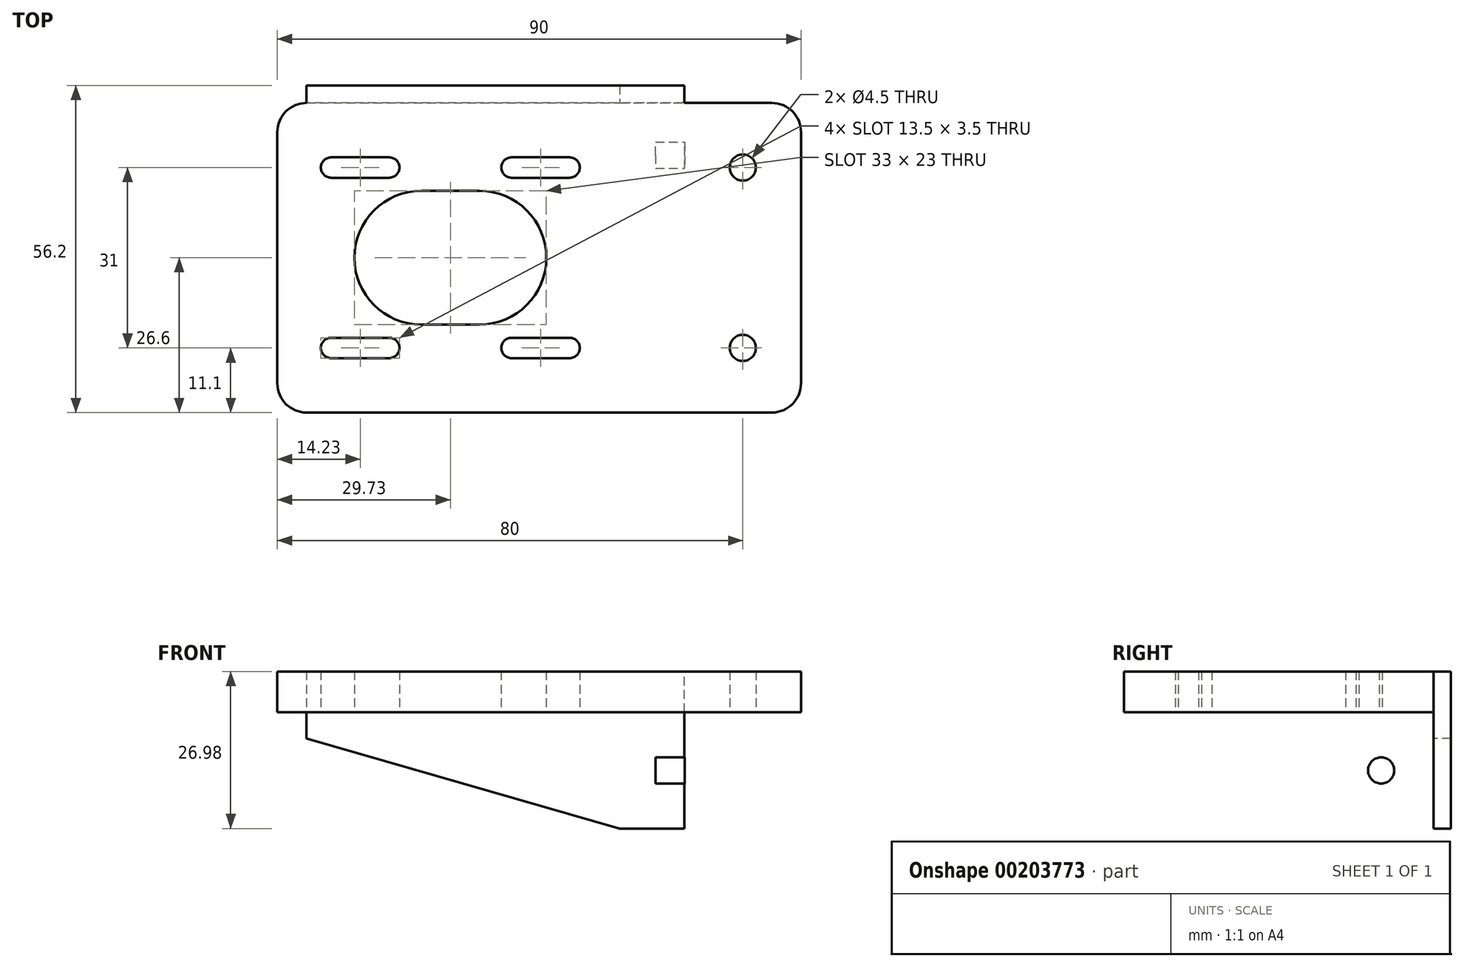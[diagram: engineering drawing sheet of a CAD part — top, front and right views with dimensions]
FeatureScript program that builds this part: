
annotation { "Feature Type Name" : "Feature", "Feature Type Description" : "" }
export const myFeature = defineFeature(function(context is Context, id is Id, definition is map)
    precondition{}
    {
        {
            var Q0;
            Q0=qCreatedBy(makeId("Top.planeOp"),FACE);
            var sketch = newSketch(context, id + "F0", { "sketchPlane" : qUnion([Q0])});
            skLineSegment(sketch, "E0.bottom", {"start": v(45, 26.6) * mm, "end": v(-45, 26.6) * mm});
            skLineSegment(sketch, "E0.top", {"start": v(45, -26.6) * mm, "end": v(-45, -26.6) * mm});
            skLineSegment(sketch, "E0.left", {"start": v(45, 26.6) * mm, "end": v(45, -26.6) * mm});
            skLineSegment(sketch, "E0.right", {"start": v(-45, 26.6) * mm, "end": v(-45, -26.6) * mm});
            skPoint(sketch, "E0.middle", {"position": v(0, 0) * mm});
            skLineSegment(sketch, "E1", {"start": v(-45, 0) * mm, "end": v(-10.27, 0) * mm, "construction": true});
            skLineSegment(sketch, "E2", {"start": v(-10.27, 0) * mm, "end": v(-10.27, 15.5) * mm, "construction": true});
            skLineSegment(sketch, "E3", {"start": v(-10.27, 15.5) * mm, "end": v(5.23, 15.5) * mm, "construction": true});
            skLineSegment(sketch, "E4", {"start": v(5.23, 15.5) * mm, "end": v(35, 15.5) * mm, "construction": true});
            skArc(sketch, "E5", {"start": v(-10.27, -11.5) * mm, "mid": v(1.23, 0) * mm, "end": v(-10.27, 11.5) * mm});
            skArc(sketch, "E6", {"start": v(5.23, 13.75) * mm, "mid": v(6.98, 15.5) * mm, "end": v(5.23, 17.25) * mm});
            skCircle(sketch, "E7", {"center": v(35, 15.5) * mm, "radius": 2.25 * mm});
            skCircle(sketch, "E8.MirrorC", {"center": v(35, -15.5) * mm, "radius": 2.25 * mm});
            skLineSegment(sketch, "E9", {"start": v(-10.27, 11.5) * mm, "end": v(-20.27, 11.5) * mm});
            skLineSegment(sketch, "E10.MirrorCS", {"start": v(-10.27, -11.5) * mm, "end": v(-20.27, -11.5) * mm});
            skArc(sketch, "E11", {"start": v(-20.27, 11.5) * mm, "mid": v(-31.77, 0) * mm, "end": v(-20.27, -11.5) * mm});
            skLineSegment(sketch, "E12", {"start": v(5.23, 15.5) * mm, "end": v(5.23, 10.19) * mm, "construction": true});
            skLineSegment(sketch, "E13", {"start": v(5.23, 13.75) * mm, "end": v(-4.77, 13.75) * mm});
            skLineSegment(sketch, "E14.MirrorCS", {"start": v(5.23, 17.25) * mm, "end": v(-4.77, 17.25) * mm});
            skLineSegment(sketch, "E15", {"start": v(-4.77, 13.75) * mm, "end": v(-4.77, 20.1) * mm, "construction": true});
            skArc(sketch, "E16", {"start": v(-4.77, 17.25) * mm, "mid": v(-6.52, 15.5) * mm, "end": v(-4.77, 13.75) * mm});
            skLineSegment(sketch, "E17", {"start": v(-15.27, 11.5) * mm, "end": v(-15.27, 24.74) * mm, "construction": true});
            skLineSegment(sketch, "E18.MirrorCS", {"start": v(-35.77, 13.75) * mm, "end": v(-25.77, 13.75) * mm});
            skArc(sketch, "E19.MirrorCS", {"start": v(-35.77, 13.75) * mm, "mid": v(-37.52, 15.5) * mm, "end": v(-35.77, 17.25) * mm});
            skLineSegment(sketch, "E20.MirrorCS", {"start": v(-35.77, 17.25) * mm, "end": v(-25.77, 17.25) * mm});
            skArc(sketch, "E21.MirrorCS", {"start": v(-25.77, 17.25) * mm, "mid": v(-24.02, 15.5) * mm, "end": v(-25.77, 13.75) * mm});
            skArc(sketch, "E22.MirrorCS", {"start": v(5.23, -13.75) * mm, "mid": v(6.98, -15.5) * mm, "end": v(5.23, -17.25) * mm});
            skLineSegment(sketch, "E23.MirrorCS", {"start": v(5.23, -17.25) * mm, "end": v(-4.77, -17.25) * mm});
            skArc(sketch, "E24.MirrorCS", {"start": v(-4.77, -17.25) * mm, "mid": v(-6.52, -15.5) * mm, "end": v(-4.77, -13.75) * mm});
            skLineSegment(sketch, "E25.MirrorCS", {"start": v(5.23, -13.75) * mm, "end": v(-4.77, -13.75) * mm});
            skArc(sketch, "E26.MirrorCS", {"start": v(-35.77, -13.75) * mm, "mid": v(-37.52, -15.5) * mm, "end": v(-35.77, -17.25) * mm});
            skLineSegment(sketch, "E27.MirrorCS", {"start": v(-35.77, -13.75) * mm, "end": v(-25.77, -13.75) * mm});
            skArc(sketch, "E28.MirrorCS", {"start": v(-25.77, -17.25) * mm, "mid": v(-24.02, -15.5) * mm, "end": v(-25.77, -13.75) * mm});
            skLineSegment(sketch, "E29.MirrorCS", {"start": v(-35.77, -17.25) * mm, "end": v(-25.77, -17.25) * mm});
            skSolve(sketch);
        }
        {
            var Q0;
            Q0=makeQuery(id+"F0.imprint","IMPRINT",FACE,{"disambiguationData":[TD([[makeQuery(id+"F0.imprint","IMPRINT",EDGE,{"derivedFrom":sQuery(id+"F0.wireOp",EDGE,"E0.bottom")}),1.0]])]});
            extrude(context, id + "F1", {"entities" : qUnion([Q0]), "depth" : 7 * mm, "symmetric" : true});
        }
        {
            var Q0;
            Q0=makeQuery(id+"F1.opExtrude","SWEPT_EDGE",EDGE,{"disambiguationData":[OSD([sQuery(id+"F0.wireOp",EDGE,"E0.bottom"),sQuery(id+"F0.wireOp",EDGE,"E0.right")])]});
            var Q1;
            Q1=makeQuery(id+"F1.opExtrude","SWEPT_EDGE",EDGE,{"disambiguationData":[OSD([sQuery(id+"F0.wireOp",EDGE,"E0.top"),sQuery(id+"F0.wireOp",EDGE,"E0.right")])]});
            var Q2;
            Q2=makeQuery(id+"F1.opExtrude","SWEPT_EDGE",EDGE,{"disambiguationData":[OSD([sQuery(id+"F0.wireOp",EDGE,"E0.top"),sQuery(id+"F0.wireOp",EDGE,"E0.left")])]});
            var Q3;
            Q3=makeQuery(id+"F1.opExtrude","SWEPT_EDGE",EDGE,{"disambiguationData":[OSD([sQuery(id+"F0.wireOp",EDGE,"E0.bottom"),sQuery(id+"F0.wireOp",EDGE,"E0.left")])]});
            fillet(context, id + "F2", {"entities" : qUnion([Q0, Q1, Q2, Q3]), "radius" : 5 * mm, "tangentPropagation" : true, "allowEdgeOverflow" : false});
        }
        {
            var Q0;
            Q0=qCreatedBy(makeId("Front.planeOp"),FACE);
            var sketch = newSketch(context, id + "F3", { "sketchPlane" : qUnion([Q0])});
            skLineSegment(sketch, "E30", {"start": v(0, 0) * mm, "end": v(25, 0) * mm, "construction": true});
            skLineSegment(sketch, "E31", {"start": v(25, 0) * mm, "end": v(25, -23.5) * mm, "construction": true});
            skLineSegment(sketch, "E32", {"start": v(25, -23.5) * mm, "end": v(20, -23.5) * mm});
            skLineSegment(sketch, "E33", {"start": v(20, -23.5) * mm, "end": v(20, -3.5) * mm});
            skLineSegment(sketch, "E34", {"start": v(20, -3.5) * mm, "end": v(25, -3.5) * mm});
            skLineSegment(sketch, "E35", {"start": v(25, -3.5) * mm, "end": v(25, -23.5) * mm});
            skSolve(sketch);
        }
        {
            var Q0;
            Q0=makeQuery(id+"F3.imprint","IMPRINT",FACE,{"disambiguationData":[TD([[makeQuery(id+"F3.imprint","IMPRINT",EDGE,{"derivedFrom":sQuery(id+"F3.wireOp",EDGE,"E32")}),-1.0]])]});
            extrude(context, id + "F4", {"entities" : qUnion([Q0]), "operationType" : NewBodyOperationType.ADD, "depth" : 53.2 * mm, "symmetric" : true});
        }
        {
            var Q0;
            Q0=makeQuery(id+"F4.boolean.opBoolean","MERGE",FACE,{"derivedFrom":[makeQuery(id+"F1.opExtrude","SWEPT_FACE",FACE,{"disambiguationData":[OSD([sQuery(id+"F0.wireOp",EDGE,"E0.top")])]}),makeQuery(id+"F4.opExtrude","CAP_FACE",FACE,{"disambiguationData":[OSD([sQuery(id+"F3.wireOp",EDGE,"E32"),sQuery(id+"F3.wireOp",EDGE,"E33"),sQuery(id+"F3.wireOp",EDGE,"E34"),sQuery(id+"F3.wireOp",EDGE,"E35")])],"isStart":false})]});
            var sketch = newSketch(context, id + "F5", { "sketchPlane" : qUnion([Q0])});
            skLineSegment(sketch, "E36", {"start": v(25, -23.5) * mm, "end": v(25, 3.5) * mm});
            skLineSegment(sketch, "E37", {"start": v(25, 3.5) * mm, "end": v(-40, 3.5) * mm});
            skLineSegment(sketch, "E38", {"start": v(-40, 3.5) * mm, "end": v(-40, -8.5) * mm});
            skLineSegment(sketch, "E39", {"start": v(-40, -8.5) * mm, "end": v(13.87, -23.5) * mm});
            skLineSegment(sketch, "E40", {"start": v(13.87, -23.5) * mm, "end": v(25, -23.5) * mm});
            skSolve(sketch);
        }
        {
            var Q0;
            {var subQ3=sQuery(id+"F5.wireOp",EDGE,"E39");Q0=makeQuery(id+"F5.imprint","IMPRINT",FACE,{"disambiguationData":[TD([[makeQuery(id+"F5.imprint","IMPRINT",EDGE,{"derivedFrom":subQ3}),1.0]])]});}
            var Q1;
            {var subQ11=sQuery(id+"F5.wireOp",EDGE,"E37");Q1=makeQuery(id+"F5.imprint","IMPRINT",FACE,{"disambiguationData":[TD([[makeQuery(id+"F5.imprint","IMPRINT",EDGE,{"derivedFrom":subQ11}),1.0]])]});}
            extrude(context, id + "F6", {"entities" : qUnion([Q0, Q1]), "operationType" : NewBodyOperationType.ADD, "depth" : 3 * mm});
        }
        {
            var Q0;
            Q0=makeQuery(id+"F4.boolean.opBoolean","MERGE",FACE,{"derivedFrom":[makeQuery(id+"F1.opExtrude","SWEPT_FACE",FACE,{"disambiguationData":[OSD([sQuery(id+"F0.wireOp",EDGE,"E0.bottom")])]}),makeQuery(id+"F4.opExtrude","CAP_FACE",FACE,{"disambiguationData":[OSD([sQuery(id+"F3.wireOp",EDGE,"E32"),sQuery(id+"F3.wireOp",EDGE,"E33"),sQuery(id+"F3.wireOp",EDGE,"E34"),sQuery(id+"F3.wireOp",EDGE,"E35")])],"isStart":true})]});
            var sketch = newSketch(context, id + "F7", { "sketchPlane" : qUnion([Q0])});
            skLineSegment(sketch, "E41", {"start": v(-24.96, -23.48) * mm, "end": v(-24.96, 3.5) * mm});
            skLineSegment(sketch, "E42", {"start": v(-24.96, 3.5) * mm, "end": v(40, 3.5) * mm});
            skLineSegment(sketch, "E43", {"start": v(40, 3.5) * mm, "end": v(40, -8.02) * mm});
            skLineSegment(sketch, "E44", {"start": v(40, -8.02) * mm, "end": v(-13.87, -23.48) * mm});
            skLineSegment(sketch, "E45", {"start": v(-13.87, -23.48) * mm, "end": v(-24.96, -23.48) * mm});
            skSolve(sketch);
        }
        {
            var Q0;
            {var subQ9=sQuery(id+"F7.wireOp",EDGE,"E41");Q0=makeQuery(id+"F7.imprint","IMPRINT",FACE,{"disambiguationData":[TD([[makeQuery(id+"F7.imprint","IMPRINT",EDGE,{"derivedFrom":subQ9}),-1.0]])]});}
            var Q1;
            {var subQ1=sQuery(id+"F7.wireOp",EDGE,"E44");Q1=makeQuery(id+"F7.imprint","IMPRINT",FACE,{"disambiguationData":[TD([[makeQuery(id+"F7.imprint","IMPRINT",EDGE,{"derivedFrom":subQ1}),-1.0]])]});}
            extrude(context, id + "F8", {"entities" : qUnion([Q0, Q1]), "operationType" : NewBodyOperationType.ADD, "depth" : 3 * mm});
        }
        {
            var Q0;
            Q0=makeQuery(id+"F6.boolean.opBoolean","MERGE",FACE,{"derivedFrom":[makeQuery(id+"F4.opExtrude","SWEPT_FACE",FACE,{"disambiguationData":[OSD([sQuery(id+"F3.wireOp",EDGE,"E35")])]}),makeQuery(id+"F6.opExtrude","SWEPT_FACE",FACE,{"disambiguationData":[OSD([sQuery(id+"F5.wireOp",EDGE,"E36")])]})]});
            var sketch = newSketch(context, id + "F9", { "sketchPlane" : qUnion([Q0])});
            skLineSegment(sketch, "E46", {"start": v(-29.6, -23.5) * mm, "end": v(-29.6, -13.5) * mm, "construction": true});
            skLineSegment(sketch, "E47", {"start": v(-29.6, -13.5) * mm, "end": v(-17.6, -13.5) * mm, "construction": true});
            skLineSegment(sketch, "E48", {"start": v(0, 0) * mm, "end": v(0, -35.76) * mm, "construction": true});
            skPoint(sketch, "E48.endSnap0", {"position": v(0, -3.5) * mm});
            skCircle(sketch, "E49", {"center": v(-17.6, -13.5) * mm, "radius": 2.25 * mm});
            skCircle(sketch, "E50.MirrorC", {"center": v(17.6, -13.5) * mm, "radius": 2.25 * mm});
            skSolve(sketch);
        }
        {
            var Q0;
            Q0=makeQuery(id+"F9.imprint","IMPRINT",FACE,{"disambiguationData":[TD([[makeQuery(id+"F9.imprint","IMPRINT",EDGE,{"derivedFrom":sQuery(id+"F9.wireOp",EDGE,"E49")}),1.0]])]});
            var Q1;
            Q1=makeQuery(id+"F9.imprint","IMPRINT",FACE,{"disambiguationData":[TD([[makeQuery(id+"F9.imprint","IMPRINT",EDGE,{"derivedFrom":sQuery(id+"F9.wireOp",EDGE,"E50.MirrorC")}),-1.0]])]});
            extrude(context, id + "F10", {"entities" : qUnion([Q0, Q1]), "operationType" : NewBodyOperationType.REMOVE, "endBound" : BoundingType.UP_TO_NEXT, "oppositeDirection" : true, "depth" : 25 * mm});
        }
    });
